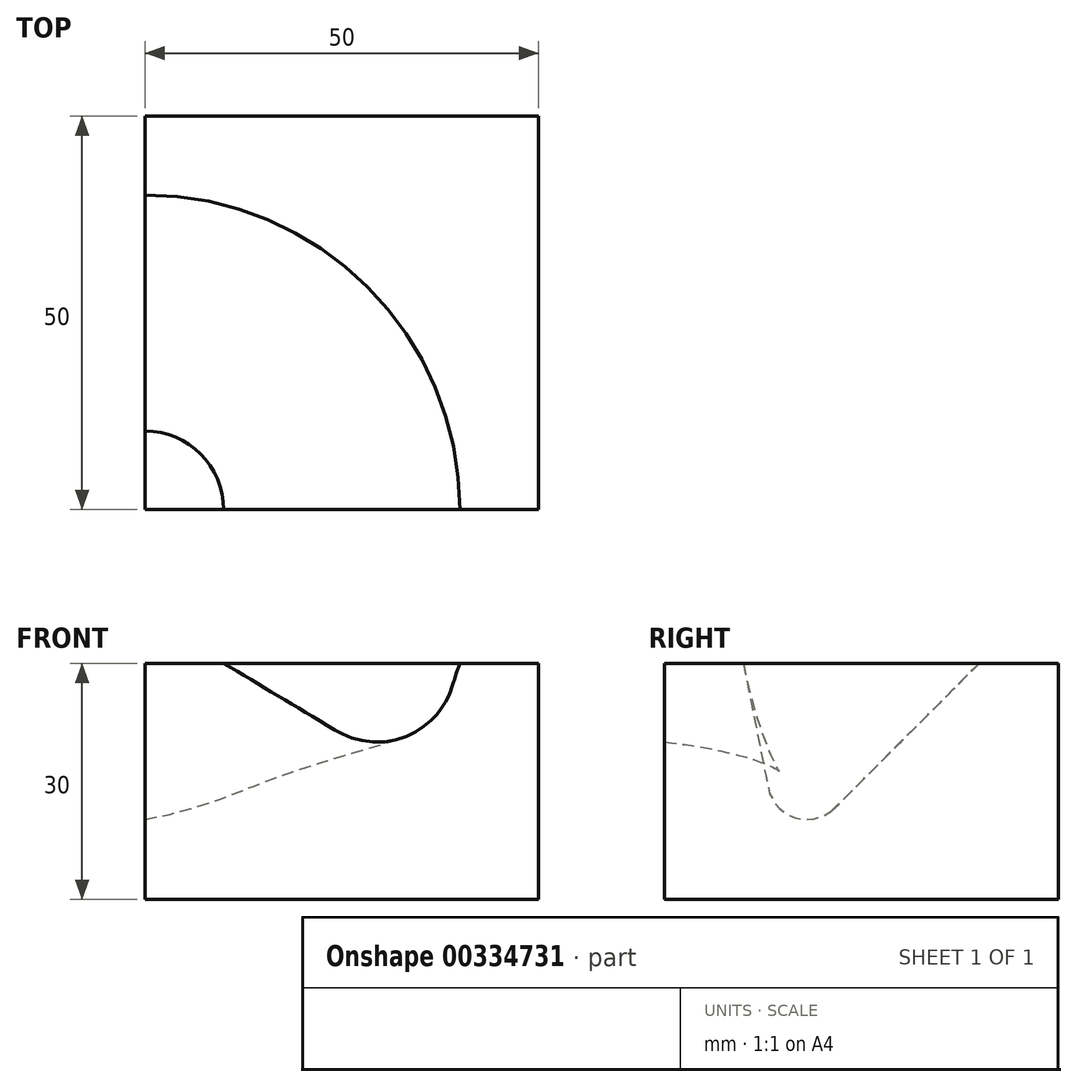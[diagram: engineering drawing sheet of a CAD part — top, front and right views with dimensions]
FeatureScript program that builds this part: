
annotation { "Feature Type Name" : "Feature", "Feature Type Description" : "" }
export const myFeature = defineFeature(function(context is Context, id is Id, definition is map)
    precondition{}
    {
        {
            var Q0;
            Q0=qCreatedBy(makeId("Top.planeOp"),FACE);
            var sketch = newSketch(context, id + "F0", { "sketchPlane" : qUnion([Q0])});
            skLineSegment(sketch, "E0.bottom", {"start": v(25, 25) * mm, "end": v(-25, 25) * mm});
            skLineSegment(sketch, "E0.top", {"start": v(25, -25) * mm, "end": v(-25, -25) * mm});
            skLineSegment(sketch, "E0.left", {"start": v(25, 25) * mm, "end": v(25, -25) * mm});
            skLineSegment(sketch, "E0.right", {"start": v(-25, 25) * mm, "end": v(-25, -25) * mm});
            skPoint(sketch, "E0.middle", {"position": v(0, 0) * mm});
            skSolve(sketch);
        }
        {
            var Q0;
            Q0=makeQuery(id+"F0.imprint","IMPRINT",FACE,{"disambiguationData":[TD([[makeQuery(id+"F0.imprint","IMPRINT",EDGE,{"derivedFrom":sQuery(id+"F0.wireOp",EDGE,"E0.bottom")}),1.0]])]});
            extrude(context, id + "F1", {"entities" : qUnion([Q0]), "depth" : 30 * mm});
        }
        {
            var Q0;
            Q0=makeQuery(id+"F1.opExtrude","SWEPT_FACE",FACE,{"disambiguationData":[OSD([sQuery(id+"F0.wireOp",EDGE,"E0.top")])]});
            var sketch = newSketch(context, id + "F2", { "sketchPlane" : qUnion([Q0])});
            skLineSegment(sketch, "E1", {"start": v(-15, 30) * mm, "end": v(-0.69, 21.41) * mm});
            skLineSegment(sketch, "E2", {"start": v(13.94, 26.83) * mm, "end": v(15, 30) * mm});
            skPoint(sketch, "E3.visualSharp", {"position": v(10, 15) * mm});
            skArc(sketch, "E3.filletArc", {"start": v(-0.69, 21.41) * mm, "mid": v(7.92, 20.6) * mm, "end": v(13.94, 26.83) * mm});
            skSolve(sketch);
        }
        {
            var Q0;
            Q0=makeQuery(id+"F1.opExtrude","SWEPT_FACE",FACE,{"disambiguationData":[OSD([sQuery(id+"F0.wireOp",EDGE,"E0.right")])]});
            var sketch = newSketch(context, id + "F3", { "sketchPlane" : qUnion([Q0])});
            skLineSegment(sketch, "E4", {"start": v(-15, 30) * mm, "end": v(3.4, 11.6) * mm});
            skLineSegment(sketch, "E5", {"start": v(11.83, 14.16) * mm, "end": v(15, 30) * mm});
            skPoint(sketch, "E6.visualSharp", {"position": v(10, 5) * mm});
            skArc(sketch, "E6.filletArc", {"start": v(3.4, 11.6) * mm, "mid": v(8.38, 10.36) * mm, "end": v(11.83, 14.16) * mm});
            skSolve(sketch);
        }
        {
            var Q0;
            Q0=makeQuery(id+"F1.opExtrude","CAP_FACE",FACE,{"disambiguationData":[OSD([sQuery(id+"F0.wireOp",EDGE,"E0.bottom"),sQuery(id+"F0.wireOp",EDGE,"E0.top"),sQuery(id+"F0.wireOp",EDGE,"E0.left"),sQuery(id+"F0.wireOp",EDGE,"E0.right")])],"isStart":false});
            var sketch = newSketch(context, id + "F4", { "sketchPlane" : qUnion([Q0])});
            skCircle(sketch, "E7", {"center": v(-25, -25) * mm, "radius": 10 * mm});
            skCircle(sketch, "E8", {"center": v(-25, -25) * mm, "radius": 40 * mm});
            skSolve(sketch);
        }
        {
            var Q1;
            {var subQ0=sQuery(id+"F2.wireOp",EDGE,"E1");Q1=makeQuery(id+"F2.imprint","IMPRINT",FACE,{"disambiguationData":[TD([[makeQuery(id+"F2.imprint","IMPRINT",EDGE,{"derivedFrom":subQ0}),1.0]])]});}
            var Q2;
            {var subQ0=sQuery(id+"F3.wireOp",EDGE,"E4");Q2=makeQuery(id+"F3.imprint","IMPRINT",FACE,{"disambiguationData":[TD([[makeQuery(id+"F3.imprint","IMPRINT",EDGE,{"derivedFrom":subQ0}),1.0]])]});}
            var Q3;
            Q3=sQuery(id+"F4.wireOp",EDGE,"E7");
            var Q4;
            Q4=sQuery(id+"F4.wireOp",EDGE,"E8");
            loft(context, id + "F5", {"operationType" : NewBodyOperationType.REMOVE, "addGuides" : true, "sheetProfilesArray" : [{ "sheetProfileEntities" : qUnion([Q1]) }, { "sheetProfileEntities" : qUnion([Q2]) }], "guidesArray" : [{ "guideEntities" : qUnion([Q3]), "guideDerivativeType" : LoftGuideDerivativeType.DEFAULT, "guideDerivativeMagnitude" : 1 }, { "guideEntities" : qUnion([Q4]), "guideDerivativeType" : LoftGuideDerivativeType.DEFAULT, "guideDerivativeMagnitude" : 1 }]});
        }
    });
